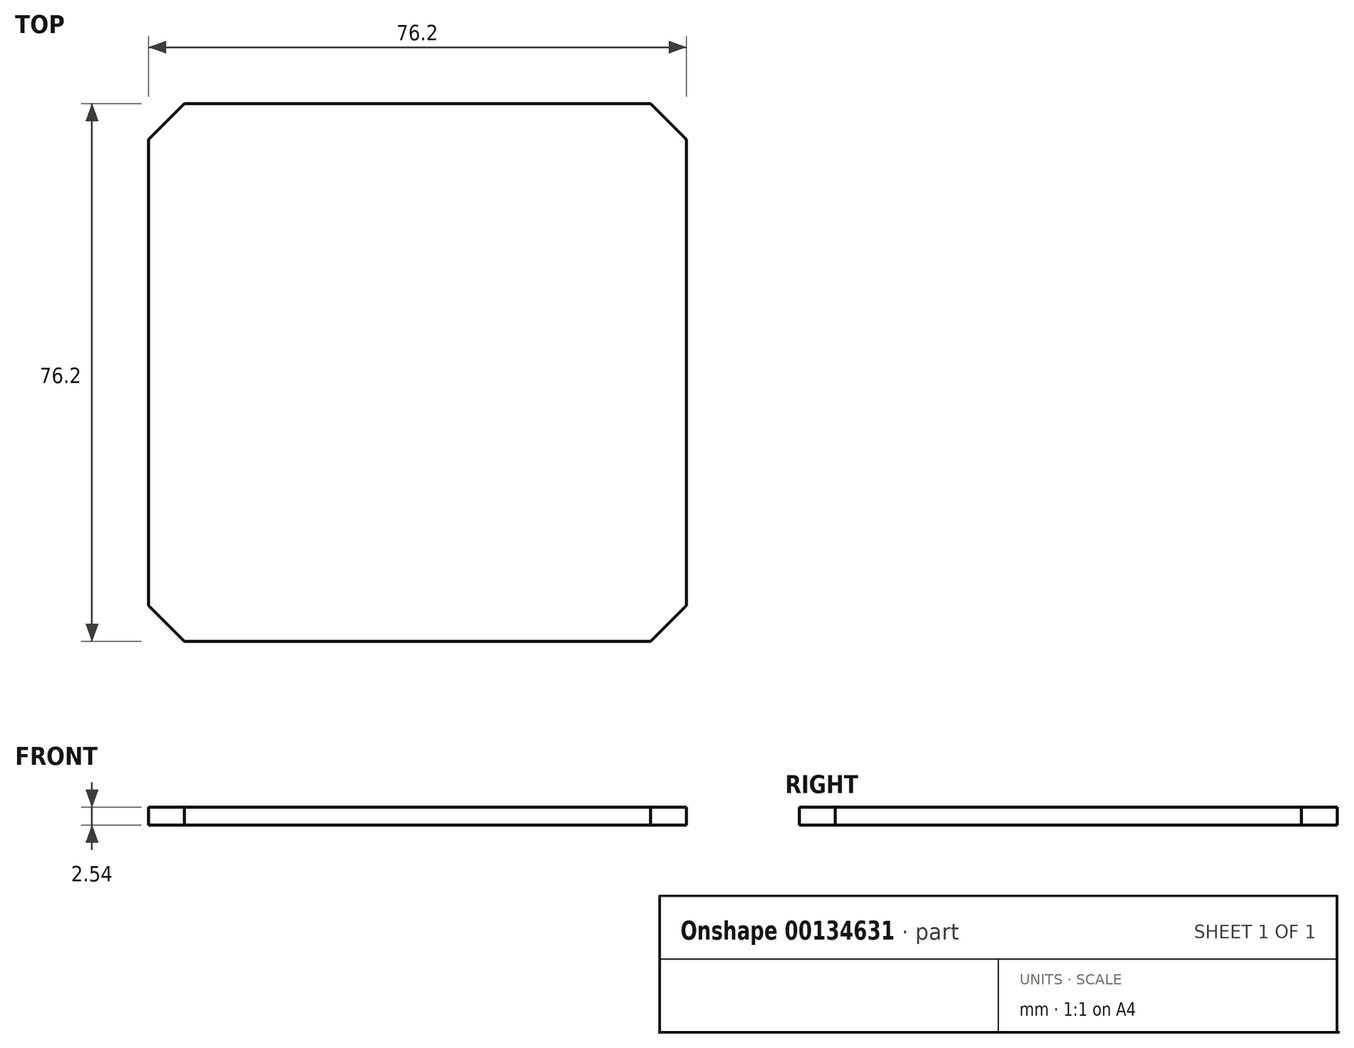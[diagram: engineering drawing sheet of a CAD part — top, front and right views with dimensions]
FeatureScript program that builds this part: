
annotation { "Feature Type Name" : "Feature", "Feature Type Description" : "" }
export const myFeature = defineFeature(function(context is Context, id is Id, definition is map)
    precondition{}
    {
        {
            var Q0;
            Q0=qCreatedBy(makeId("Top.planeOp"),FACE);
            var sketch = newSketch(context, id + "F0", { "sketchPlane" : qUnion([Q0])});
            skLineSegment(sketch, "E0.bottom", {"start": v(-15.5, -37.1) * mm, "end": v(-91.7, -37.1) * mm});
            skLineSegment(sketch, "E0.top", {"start": v(-15.5, 39.1) * mm, "end": v(-91.7, 39.1) * mm});
            skLineSegment(sketch, "E0.left", {"start": v(-15.5, -37.1) * mm, "end": v(-15.5, 39.1) * mm});
            skLineSegment(sketch, "E0.right", {"start": v(-91.7, -37.1) * mm, "end": v(-91.7, 39.1) * mm});
            skPoint(sketch, "E0.middle", {"position": v(-53.6, 1) * mm});
            skSolve(sketch);
        }
        {
            var Q0;
            Q0 = qSketchRegion(id + "F0", true);
            extrude(context, id + "F1", {"entities" : qUnion([Q0]), "depth" : 2.54 * mm});
        }
        {
            var Q0;
            Q0=makeQuery(id+"F1.opExtrude","SWEPT_BODY",BODY,{"disambiguationData":[OSD([sQuery(id+"F0.wireOp",EDGE,"E0.bottom"),sQuery(id+"F0.wireOp",EDGE,"E0.top"),sQuery(id+"F0.wireOp",EDGE,"E0.left"),sQuery(id+"F0.wireOp",EDGE,"E0.right")])]});
            deleteBodies(context, id + "F2", {"entities" : qUnion([Q0])});
        }
        {
            var Q0;
            Q0=qCreatedBy(makeId("Top.planeOp"),FACE);
            var sketch = newSketch(context, id + "F3", { "sketchPlane" : qUnion([Q0])});
            skLineSegment(sketch, "E1.bottom", {"start": v(38.1, 38.1) * mm, "end": v(-38.1, 38.1) * mm});
            skLineSegment(sketch, "E1.top", {"start": v(38.1, -38.1) * mm, "end": v(-38.1, -38.1) * mm});
            skLineSegment(sketch, "E1.left", {"start": v(38.1, 38.1) * mm, "end": v(38.1, -38.1) * mm});
            skLineSegment(sketch, "E1.right", {"start": v(-38.1, 38.1) * mm, "end": v(-38.1, -38.1) * mm});
            skPoint(sketch, "E1.middle", {"position": v(0, 0) * mm});
            skSolve(sketch);
        }
        {
            var Q0;
            Q0 = qSketchRegion(id + "F3", true);
            extrude(context, id + "F4", {"entities" : qUnion([Q0]), "depth" : 2.54 * mm});
        }
        {
            var Q0;
            Q0=makeQuery(id+"F4.opExtrude","SWEPT_EDGE",EDGE,{"disambiguationData":[OSD([sQuery(id+"F3.wireOp",EDGE,"E1.top"),sQuery(id+"F3.wireOp",EDGE,"E1.right")])]});
            var Q1;
            Q1=makeQuery(id+"F4.opExtrude","SWEPT_EDGE",EDGE,{"disambiguationData":[OSD([sQuery(id+"F3.wireOp",EDGE,"E1.bottom"),sQuery(id+"F3.wireOp",EDGE,"E1.right")])]});
            var Q2;
            Q2=makeQuery(id+"F4.opExtrude","SWEPT_EDGE",EDGE,{"disambiguationData":[OSD([sQuery(id+"F3.wireOp",EDGE,"E1.bottom"),sQuery(id+"F3.wireOp",EDGE,"E1.left")])]});
            var Q3;
            Q3=makeQuery(id+"F4.opExtrude","SWEPT_EDGE",EDGE,{"disambiguationData":[OSD([sQuery(id+"F3.wireOp",EDGE,"E1.top"),sQuery(id+"F3.wireOp",EDGE,"E1.left")])]});
            chamfer(context, id + "F5", {"entities" : qUnion([Q0, Q1, Q2, Q3]), "width" : 5.08 * mm, "tangentPropagation" : true});
        }
    });
